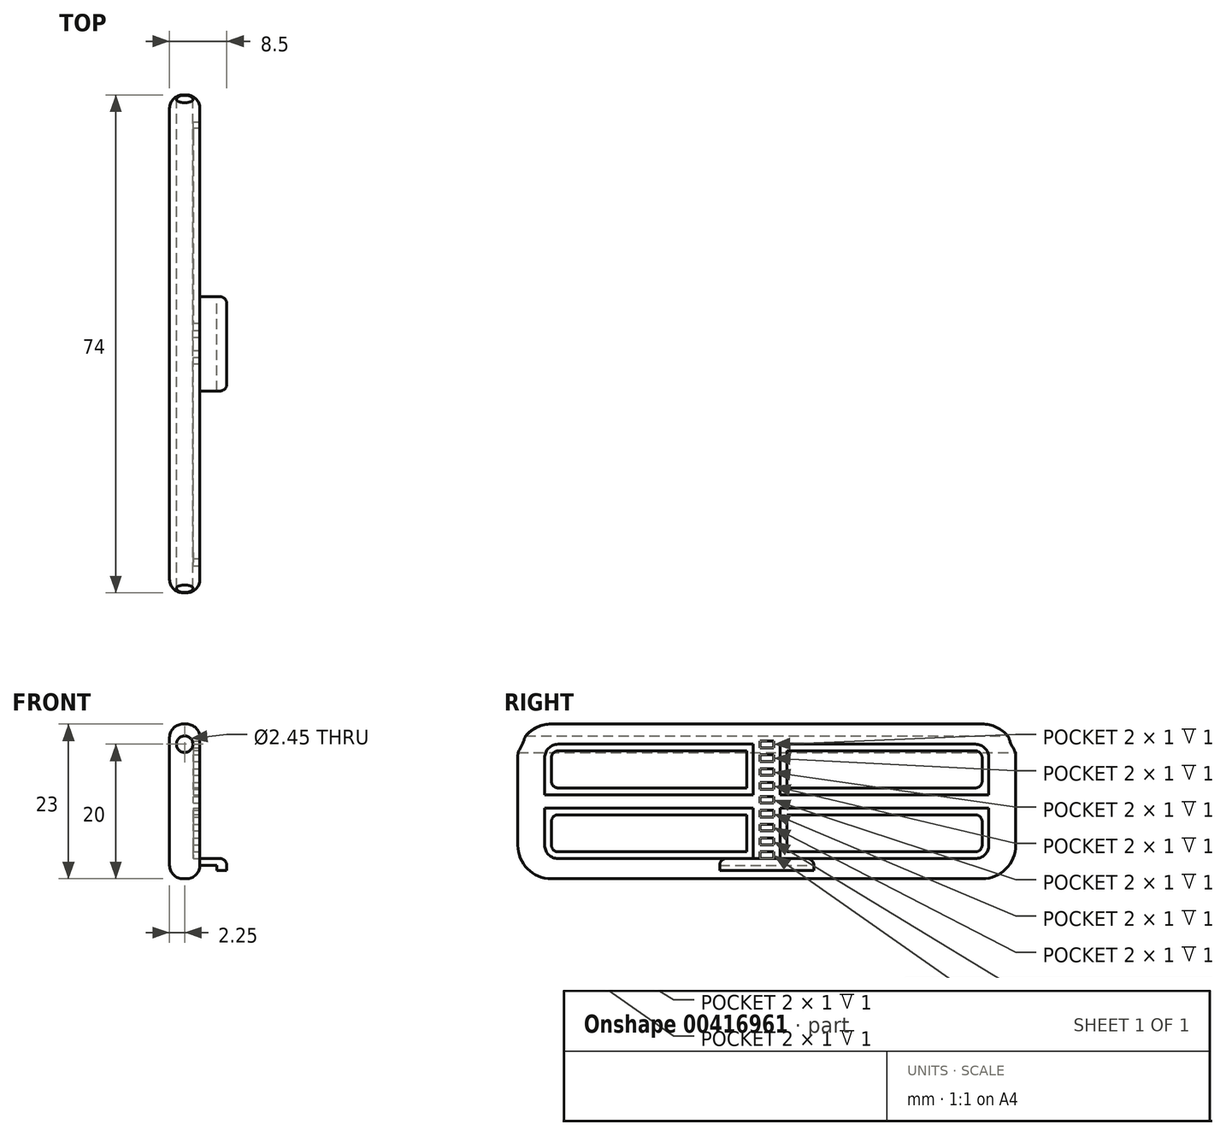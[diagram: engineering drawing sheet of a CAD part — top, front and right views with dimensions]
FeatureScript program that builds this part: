
annotation { "Feature Type Name" : "Feature", "Feature Type Description" : "" }
export const myFeature = defineFeature(function(context is Context, id is Id, definition is map)
    precondition{}
    {
        {
            var Q0;
            Q0=qCreatedBy(makeId("Right.planeOp"),FACE);
            var sketch = newSketch(context, id + "F0", { "sketchPlane" : qUnion([Q0])});
            skLineSegment(sketch, "E0.bottom", {"start": v(5, 0) * mm, "end": v(69, 0) * mm});
            skLineSegment(sketch, "E0.top", {"start": v(5, 23) * mm, "end": v(69, 23) * mm});
            skLineSegment(sketch, "E0.left", {"start": v(0, 5) * mm, "end": v(0, 18) * mm});
            skLineSegment(sketch, "E0.right", {"start": v(74, 5) * mm, "end": v(74, 18) * mm});
            skPoint(sketch, "E1.visualSharp", {"position": v(0, 23) * mm});
            skArc(sketch, "E1.filletArc", {"start": v(5, 23) * mm, "mid": v(1.46, 21.54) * mm, "end": v(0, 18) * mm});
            skPoint(sketch, "E2.visualSharp", {"position": v(74, 23) * mm});
            skArc(sketch, "E2.filletArc", {"start": v(74, 18) * mm, "mid": v(72.54, 21.54) * mm, "end": v(69, 23) * mm});
            skPoint(sketch, "E3.visualSharp", {"position": v(74, 0) * mm});
            skArc(sketch, "E3.filletArc", {"start": v(69, 0) * mm, "mid": v(72.54, 1.46) * mm, "end": v(74, 5) * mm});
            skPoint(sketch, "E4.visualSharp", {"position": v(0, 0) * mm});
            skArc(sketch, "E4.filletArc", {"start": v(0, 5) * mm, "mid": v(1.46, 1.46) * mm, "end": v(5, 0) * mm});
            skSolve(sketch);
        }
        {
            var Q0;
            Q0 = qSketchRegion(id + "F0", true);
            extrude(context, id + "F1", {"entities" : qUnion([Q0]), "depth" : 4.5 * mm});
        }
        {
            var Q0;
            Q0=makeQuery(id+"F1.opExtrude","SWEPT_FACE",FACE,{"disambiguationData":[OSD([sQuery(id+"F0.wireOp",EDGE,"E0.right")])]});
            var sketch = newSketch(context, id + "F2", { "sketchPlane" : qUnion([Q0])});
            skCircle(sketch, "E5", {"center": v(-2.25, 20) * mm, "radius": 1.23 * mm});
            skSolve(sketch);
        }
        {
            var Q0;
            Q0 = qSketchRegion(id + "F2", true);
            var Q1;
            Q1=makeQuery(id+"F1.opExtrude","SWEPT_FACE",FACE,{"disambiguationData":[OSD([sQuery(id+"F0.wireOp",EDGE,"E0.left")])]});
            extrude(context, id + "F3", {"entities" : qUnion([Q0]), "operationType" : NewBodyOperationType.REMOVE, "endBound" : BoundingType.UP_TO_SURFACE, "oppositeDirection" : true, "endBoundEntityFace" : qUnion([Q1]), "depth" : 25 * mm});
        }
        {
            var Q0;
            Q0=makeQuery(id+"F1.opExtrude","CAP_EDGE",EDGE,{"disambiguationData":[OSD([sQuery(id+"F0.wireOp",EDGE,"E0.top")])],"isStart":true});
            var Q1;
            Q1=makeQuery(id+"F1.opExtrude","CAP_EDGE",EDGE,{"disambiguationData":[OSD([sQuery(id+"F0.wireOp",EDGE,"E0.top")])],"isStart":false});
            fillet(context, id + "F4", {"entities" : qUnion([Q0, Q1]), "radius" : 2 * mm, "tangentPropagation" : true, "allowEdgeOverflow" : false});
        }
        {
            var Q0;
            Q0=makeQuery(id+"F1.opExtrude","CAP_FACE",FACE,{"disambiguationData":[OSD([sQuery(id+"F0.wireOp",EDGE,"E0.bottom"),sQuery(id+"F0.wireOp",EDGE,"E0.top"),sQuery(id+"F0.wireOp",EDGE,"E0.left"),sQuery(id+"F0.wireOp",EDGE,"E0.right")])],"isStart":false});
            var sketch = newSketch(context, id + "F5", { "sketchPlane" : qUnion([Q0])});
            skLineSegment(sketch, "E6.bottom", {"start": v(6, 20) * mm, "end": v(35, 20) * mm});
            skLineSegment(sketch, "E6.top", {"start": v(6, 3) * mm, "end": v(35, 3) * mm});
            skLineSegment(sketch, "E6.left", {"start": v(4, 18) * mm, "end": v(4, 12.5) * mm});
            skLineSegment(sketch, "E6.right", {"start": v(35, 20) * mm, "end": v(35, 12.5) * mm});
            skLineSegment(sketch, "E7.bottom", {"start": v(39, 20) * mm, "end": v(68, 20) * mm});
            skLineSegment(sketch, "E7.top", {"start": v(39, 3) * mm, "end": v(68, 3) * mm});
            skLineSegment(sketch, "E7.left", {"start": v(39, 20) * mm, "end": v(39, 12.5) * mm});
            skLineSegment(sketch, "E7.right", {"start": v(70, 18) * mm, "end": v(70, 12.5) * mm});
            skLineSegment(sketch, "E8", {"start": v(4, 12.5) * mm, "end": v(35, 12.5) * mm});
            skLineSegment(sketch, "E9", {"start": v(4, 10.5) * mm, "end": v(35, 10.5) * mm});
            skLineSegment(sketch, "E10.trimOffspring", {"start": v(39, 12.5) * mm, "end": v(70, 12.5) * mm});
            skLineSegment(sketch, "E11.trimOffspring", {"start": v(35, 10.5) * mm, "end": v(35, 3) * mm});
            skLineSegment(sketch, "E12.trimOffspring", {"start": v(39, 10.5) * mm, "end": v(70, 10.5) * mm});
            skLineSegment(sketch, "E13.trimOffspring", {"start": v(39, 10.5) * mm, "end": v(39, 3) * mm});
            skLineSegment(sketch, "E14.trimOffspring", {"start": v(70, 10.5) * mm, "end": v(70, 5) * mm});
            skLineSegment(sketch, "E15.trimOffspring", {"start": v(4, 10.5) * mm, "end": v(4, 5) * mm});
            skLineSegment(sketch, "E16", {"start": v(37, 21) * mm, "end": v(37, 2) * mm, "construction": true});
            skLineSegment(sketch, "E17", {"start": v(2, 11.5) * mm, "end": v(72, 11.5) * mm, "construction": true});
            skPoint(sketch, "E18.visualSharp", {"position": v(4, 20) * mm});
            skArc(sketch, "E18.filletArc", {"start": v(6, 20) * mm, "mid": v(4.59, 19.41) * mm, "end": v(4, 18) * mm});
            skPoint(sketch, "E19.visualSharp", {"position": v(70, 20) * mm});
            skArc(sketch, "E19.filletArc", {"start": v(70, 18) * mm, "mid": v(69.41, 19.41) * mm, "end": v(68, 20) * mm});
            skPoint(sketch, "E20.visualSharp", {"position": v(70, 3) * mm});
            skArc(sketch, "E20.filletArc", {"start": v(68, 3) * mm, "mid": v(69.41, 3.59) * mm, "end": v(70, 5) * mm});
            skPoint(sketch, "E21.visualSharp", {"position": v(4, 3) * mm});
            skArc(sketch, "E21.filletArc", {"start": v(4, 5) * mm, "mid": v(4.59, 3.59) * mm, "end": v(6, 3) * mm});
            skSolve(sketch);
        }
        {
            var Q0;
            Q0 = qSketchRegion(id + "F5", true);
            extrude(context, id + "F6", {"entities" : qUnion([Q0]), "operationType" : NewBodyOperationType.REMOVE, "oppositeDirection" : true, "depth" : 1 * mm});
        }
        {
            var Q0;
            Q0=makeQuery(id+"F1.opExtrude","CAP_FACE",FACE,{"disambiguationData":[OSD([sQuery(id+"F0.wireOp",EDGE,"E0.bottom"),sQuery(id+"F0.wireOp",EDGE,"E0.top"),sQuery(id+"F0.wireOp",EDGE,"E0.left"),sQuery(id+"F0.wireOp",EDGE,"E0.right")])],"isStart":false});
            var sketch = newSketch(context, id + "F7", { "sketchPlane" : qUnion([Q0])});
            skLineSegment(sketch, "E22.bottom", {"start": v(36, 3) * mm, "end": v(38, 3) * mm});
            skLineSegment(sketch, "E22.top", {"start": v(36, 4) * mm, "end": v(38, 4) * mm});
            skLineSegment(sketch, "E22.left", {"start": v(36, 3) * mm, "end": v(36, 4) * mm});
            skLineSegment(sketch, "E22.right", {"start": v(38, 3) * mm, "end": v(38, 4) * mm});
            skLineSegment(sketch, "E23.1.0.0", {"start": v(36, 5.06) * mm, "end": v(38, 5.06) * mm});
            skLineSegment(sketch, "E23.1.0.1", {"start": v(36, 6.06) * mm, "end": v(38, 6.06) * mm});
            skLineSegment(sketch, "E23.1.0.2", {"start": v(36, 5.06) * mm, "end": v(36, 6.06) * mm});
            skLineSegment(sketch, "E23.1.0.3", {"start": v(38, 5.06) * mm, "end": v(38, 6.06) * mm});
            skLineSegment(sketch, "E23.2.0.0", {"start": v(36, 7.12) * mm, "end": v(38, 7.12) * mm});
            skLineSegment(sketch, "E23.2.0.1", {"start": v(36, 8.12) * mm, "end": v(38, 8.12) * mm});
            skLineSegment(sketch, "E23.2.0.2", {"start": v(36, 7.12) * mm, "end": v(36, 8.12) * mm});
            skLineSegment(sketch, "E23.2.0.3", {"start": v(38, 7.12) * mm, "end": v(38, 8.12) * mm});
            skLineSegment(sketch, "E23.direction1", {"start": v(36, 3) * mm, "end": v(36, 5.06) * mm, "construction": true});
            skLineSegment(sketch, "E24.0.3.0", {"start": v(36, 9.18) * mm, "end": v(38, 9.18) * mm});
            skLineSegment(sketch, "E24.3.3.0", {"start": v(36, 10.18) * mm, "end": v(38, 10.18) * mm});
            skLineSegment(sketch, "E24.6.3.0", {"start": v(36, 9.18) * mm, "end": v(36, 10.18) * mm});
            skLineSegment(sketch, "E24.9.3.0", {"start": v(38, 9.18) * mm, "end": v(38, 10.18) * mm});
            skLineSegment(sketch, "E24.0.4.0", {"start": v(36, 11.24) * mm, "end": v(38, 11.24) * mm});
            skLineSegment(sketch, "E24.3.4.0", {"start": v(36, 12.24) * mm, "end": v(38, 12.24) * mm});
            skLineSegment(sketch, "E24.6.4.0", {"start": v(36, 11.24) * mm, "end": v(36, 12.24) * mm});
            skLineSegment(sketch, "E24.9.4.0", {"start": v(38, 11.24) * mm, "end": v(38, 12.24) * mm});
            skLineSegment(sketch, "E25.0.5.0", {"start": v(36, 13.3) * mm, "end": v(38, 13.3) * mm});
            skLineSegment(sketch, "E25.3.5.0", {"start": v(36, 14.3) * mm, "end": v(38, 14.3) * mm});
            skLineSegment(sketch, "E25.6.5.0", {"start": v(36, 13.3) * mm, "end": v(36, 14.3) * mm});
            skLineSegment(sketch, "E25.9.5.0", {"start": v(38, 13.3) * mm, "end": v(38, 14.3) * mm});
            skLineSegment(sketch, "E25.0.6.0", {"start": v(36, 15.36) * mm, "end": v(38, 15.36) * mm});
            skLineSegment(sketch, "E25.3.6.0", {"start": v(36, 16.36) * mm, "end": v(38, 16.36) * mm});
            skLineSegment(sketch, "E25.6.6.0", {"start": v(36, 15.36) * mm, "end": v(36, 16.36) * mm});
            skLineSegment(sketch, "E25.9.6.0", {"start": v(38, 15.36) * mm, "end": v(38, 16.36) * mm});
            skLineSegment(sketch, "E25.0.7.0", {"start": v(36, 17.42) * mm, "end": v(38, 17.42) * mm});
            skLineSegment(sketch, "E25.3.7.0", {"start": v(36, 18.42) * mm, "end": v(38, 18.42) * mm});
            skLineSegment(sketch, "E25.6.7.0", {"start": v(36, 17.42) * mm, "end": v(36, 18.42) * mm});
            skLineSegment(sketch, "E25.9.7.0", {"start": v(38, 17.42) * mm, "end": v(38, 18.42) * mm});
            skLineSegment(sketch, "E26.0.8.0", {"start": v(36, 19.48) * mm, "end": v(38, 19.48) * mm});
            skLineSegment(sketch, "E26.3.8.0", {"start": v(36, 20.48) * mm, "end": v(38, 20.48) * mm});
            skLineSegment(sketch, "E26.6.8.0", {"start": v(36, 19.48) * mm, "end": v(36, 20.48) * mm});
            skLineSegment(sketch, "E26.9.8.0", {"start": v(38, 19.48) * mm, "end": v(38, 20.48) * mm});
            skSolve(sketch);
        }
        {
            var Q0;
            Q0 = qSketchRegion(id + "F7", true);
            extrude(context, id + "F8", {"entities" : qUnion([Q0]), "operationType" : NewBodyOperationType.REMOVE, "oppositeDirection" : true, "depth" : 1 * mm});
        }
        {
            var Q0;
            Q0=makeQuery(id+"F6.boolean.opBoolean","COPY",FACE,{"derivedFrom":makeQuery(id+"F6.opExtrude","CAP_FACE",FACE,{"disambiguationData":[OSD([sQuery(id+"F5.wireOp",EDGE,"E7.top"),sQuery(id+"F5.wireOp",EDGE,"E12.trimOffspring"),sQuery(id+"F5.wireOp",EDGE,"E13.trimOffspring"),sQuery(id+"F5.wireOp",EDGE,"E14.trimOffspring")])],"isStart":false})});
            var sketch = newSketch(context, id + "F9", { "sketchPlane" : qUnion([Q0])});
            skLineSegment(sketch, "E27.top", {"start": v(6, 4) * mm, "end": v(34, 4) * mm});
            skLineSegment(sketch, "E28", {"start": v(37, 2) * mm, "end": v(37, 21) * mm, "construction": true});
            skLineSegment(sketch, "E29.bottom", {"start": v(6, 9.5) * mm, "end": v(34, 9.5) * mm});
            skLineSegment(sketch, "E29.left", {"start": v(5, 8.5) * mm, "end": v(5, 5) * mm});
            skLineSegment(sketch, "E29.right", {"start": v(34, 9.5) * mm, "end": v(34, 4) * mm});
            skLineSegment(sketch, "E30.bottom", {"start": v(6, 19) * mm, "end": v(34, 19) * mm});
            skLineSegment(sketch, "E30.left", {"start": v(5, 18) * mm, "end": v(5, 14.5) * mm});
            skPoint(sketch, "E31.visualSharp", {"position": v(5, 19) * mm});
            skArc(sketch, "E31.filletArc", {"start": v(6, 19) * mm, "mid": v(5.3, 18.7) * mm, "end": v(5, 18) * mm});
            skLineSegment(sketch, "E32", {"start": v(34, 19) * mm, "end": v(34, 13.5) * mm});
            skLineSegment(sketch, "E33", {"start": v(34, 13.5) * mm, "end": v(6, 13.5) * mm});
            skPoint(sketch, "E34.orphan", {"position": v(34, 0) * mm});
            skPoint(sketch, "E35.visualSharp", {"position": v(5, 13.5) * mm});
            skArc(sketch, "E35.filletArc", {"start": v(5, 14.5) * mm, "mid": v(5.3, 13.8) * mm, "end": v(6, 13.5) * mm});
            skPoint(sketch, "E36.visualSharp", {"position": v(5, 9.5) * mm});
            skArc(sketch, "E36.filletArc", {"start": v(6, 9.5) * mm, "mid": v(5.3, 9.2) * mm, "end": v(5, 8.5) * mm});
            skPoint(sketch, "E37.visualSharp", {"position": v(5, 4) * mm});
            skArc(sketch, "E37.filletArc", {"start": v(5, 5) * mm, "mid": v(5.3, 4.3) * mm, "end": v(6, 4) * mm});
            skArc(sketch, "E38.MirrorCS", {"start": v(68, 9.5) * mm, "mid": v(68.7, 9.2) * mm, "end": v(69, 8.5) * mm});
            skArc(sketch, "E39.MirrorCS", {"start": v(69, 14.5) * mm, "mid": v(68.7, 13.8) * mm, "end": v(68, 13.5) * mm});
            skArc(sketch, "E40.MirrorCS", {"start": v(68, 19) * mm, "mid": v(68.7, 18.7) * mm, "end": v(69, 18) * mm});
            skArc(sketch, "E41.MirrorCS", {"start": v(69, 5) * mm, "mid": v(68.7, 4.3) * mm, "end": v(68, 4) * mm});
            skLineSegment(sketch, "E42.MirrorCS", {"start": v(40, 9.5) * mm, "end": v(40, 4) * mm});
            skPoint(sketch, "E43.MirrorP", {"position": v(69, 9.5) * mm});
            skLineSegment(sketch, "E44.MirrorCS", {"start": v(40, 19) * mm, "end": v(40, 13.5) * mm});
            skLineSegment(sketch, "E45.MirrorCS", {"start": v(68, 4) * mm, "end": v(40, 4) * mm});
            skLineSegment(sketch, "E46.MirrorCS", {"start": v(68, 9.5) * mm, "end": v(40, 9.5) * mm});
            skPoint(sketch, "E47.MirrorP", {"position": v(69, 13.5) * mm});
            skPoint(sketch, "E48.MirrorP", {"position": v(69, 19) * mm});
            skLineSegment(sketch, "E49.MirrorCS", {"start": v(69, 8.5) * mm, "end": v(69, 5) * mm});
            skLineSegment(sketch, "E50.MirrorCS", {"start": v(68, 19) * mm, "end": v(40, 19) * mm});
            skLineSegment(sketch, "E51.MirrorCS", {"start": v(40, 13.5) * mm, "end": v(68, 13.5) * mm});
            skPoint(sketch, "E52.MirrorP", {"position": v(69, 4) * mm});
            skLineSegment(sketch, "E53.MirrorCS", {"start": v(69, 18) * mm, "end": v(69, 14.5) * mm});
            skPoint(sketch, "E54.MirrorP", {"position": v(40, 0) * mm});
            skSolve(sketch);
        }
        {
            var Q0;
            Q0 = qSketchRegion(id + "F9", true);
            extrude(context, id + "F10", {"entities" : qUnion([Q0]), "operationType" : NewBodyOperationType.ADD, "depth" : 1 * mm, "offsetDistance" : 25 * mm});
        }
        {
            var Q0;
            Q0=makeQuery(id+"F1.opExtrude","CAP_FACE",FACE,{"disambiguationData":[OSD([sQuery(id+"F0.wireOp",EDGE,"E0.bottom"),sQuery(id+"F0.wireOp",EDGE,"E0.top"),sQuery(id+"F0.wireOp",EDGE,"E0.left"),sQuery(id+"F0.wireOp",EDGE,"E0.right"),sQuery(id+"F0.wireOp",EDGE,"E1.filletArc"),sQuery(id+"F0.wireOp",EDGE,"E2.filletArc"),sQuery(id+"F0.wireOp",EDGE,"E3.filletArc"),sQuery(id+"F0.wireOp",EDGE,"E4.filletArc")])],"isStart":false});
            var sketch = newSketch(context, id + "F11", { "sketchPlane" : qUnion([Q0])});
            skLineSegment(sketch, "E55.bottom", {"start": v(30, 3) * mm, "end": v(44, 3) * mm});
            skLineSegment(sketch, "E55.top", {"start": v(30, 2) * mm, "end": v(44, 2) * mm});
            skLineSegment(sketch, "E55.left", {"start": v(30, 3) * mm, "end": v(30, 2) * mm});
            skLineSegment(sketch, "E55.right", {"start": v(44, 3) * mm, "end": v(44, 2) * mm});
            skSolve(sketch);
        }
        {
            var Q0;
            Q0 = qSketchRegion(id + "F11", true);
            extrude(context, id + "F12", {"entities" : qUnion([Q0]), "operationType" : NewBodyOperationType.ADD, "depth" : 4 * mm, "offsetDistance" : 25 * mm});
        }
        {
            var Q0;
            Q0=makeQuery(id+"F12.opExtrude","SWEPT_FACE",FACE,{"disambiguationData":[OSD([sQuery(id+"F11.wireOp",EDGE,"E55.top")])]});
            var sketch = newSketch(context, id + "F13", { "sketchPlane" : qUnion([Q0])});
            skLineSegment(sketch, "E56.bottom", {"start": v(8.5, -30) * mm, "end": v(7, -30) * mm});
            skLineSegment(sketch, "E56.top", {"start": v(8.5, -44) * mm, "end": v(7, -44) * mm});
            skLineSegment(sketch, "E56.left", {"start": v(8.5, -30) * mm, "end": v(8.5, -44) * mm});
            skLineSegment(sketch, "E56.right", {"start": v(7, -30) * mm, "end": v(7, -44) * mm});
            skSolve(sketch);
        }
        {
            var Q0;
            Q0 = qSketchRegion(id + "F13", true);
            extrude(context, id + "F14", {"entities" : qUnion([Q0]), "operationType" : NewBodyOperationType.ADD, "depth" : .75 * mm, "offsetDistance" : 25 * mm});
        }
        {
            var Q0;
            Q0=makeQuery(id+"F12.opExtrude","CAP_EDGE",EDGE,{"disambiguationData":[OSD([sQuery(id+"F11.wireOp",EDGE,"E55.bottom")])],"isStart":false});
            var Q1;
            Q1=makeQuery(id+"F12.opExtrude","SWEPT_EDGE",EDGE,{"disambiguationData":[OSD([sQuery(id+"F5.wireOp",EDGE,"E6.top"),sQuery(id+"F11.wireOp",EDGE,"E55.bottom"),sQuery(id+"F11.wireOp",EDGE,"E55.left")])]});
            var Q2;
            Q2=makeQuery(id+"F12.opExtrude","SWEPT_EDGE",EDGE,{"disambiguationData":[OSD([sQuery(id+"F5.wireOp",EDGE,"E7.top"),sQuery(id+"F11.wireOp",EDGE,"E55.bottom"),sQuery(id+"F11.wireOp",EDGE,"E55.right")])]});
            var Q3;
            Q3=makeQuery(id+"F14.boolean.opBoolean","MERGE",EDGE,{"derivedFrom":[makeQuery(id+"F12.opExtrude","CAP_EDGE",EDGE,{"disambiguationData":[OSD([sQuery(id+"F11.wireOp",EDGE,"E55.right")])],"isStart":false}),makeQuery(id+"F14.opExtrude","SWEPT_EDGE",EDGE,{"disambiguationData":[OSD([sQuery(id+"F13.wireOp",EDGE,"E56.top"),sQuery(id+"F13.wireOp",EDGE,"E56.left")])]})]});
            var Q4;
            Q4=makeQuery(id+"F14.boolean.opBoolean","MERGE",EDGE,{"derivedFrom":[makeQuery(id+"F12.opExtrude","CAP_EDGE",EDGE,{"disambiguationData":[OSD([sQuery(id+"F11.wireOp",EDGE,"E55.left")])],"isStart":false}),makeQuery(id+"F14.opExtrude","SWEPT_EDGE",EDGE,{"disambiguationData":[OSD([sQuery(id+"F13.wireOp",EDGE,"E56.bottom"),sQuery(id+"F13.wireOp",EDGE,"E56.left")])]})]});
            fillet(context, id + "F15", {"entities" : qUnion([Q0, Q1, Q2, Q3, Q4]), "radius" : 1 * mm, "tangentPropagation" : true, "allowEdgeOverflow" : false});
        }
    });
